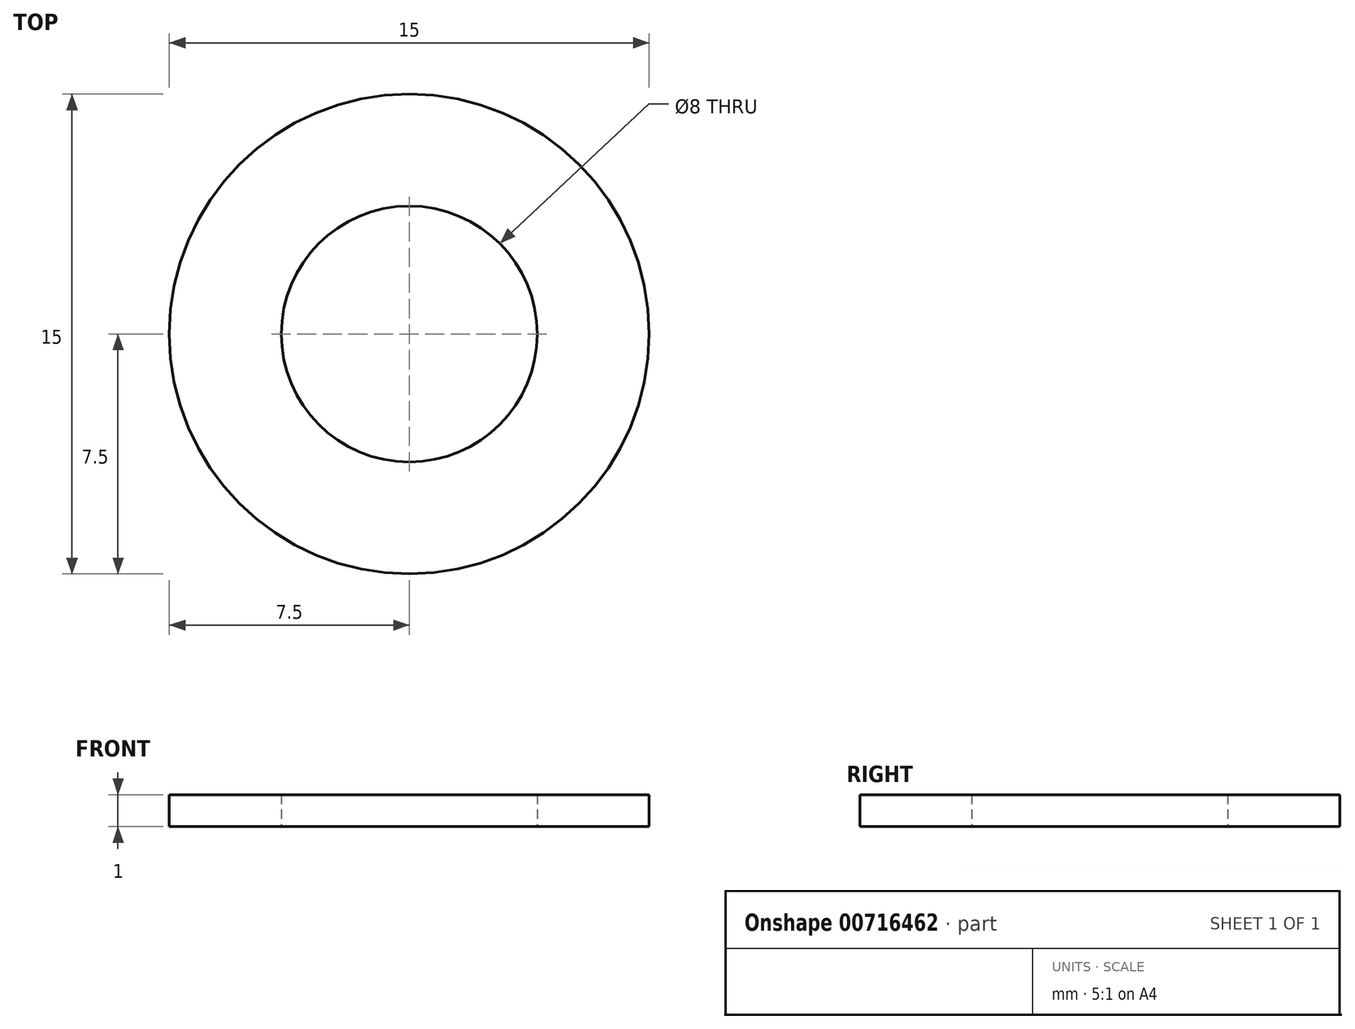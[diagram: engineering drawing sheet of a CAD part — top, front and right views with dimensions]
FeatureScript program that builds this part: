
annotation { "Feature Type Name" : "Feature", "Feature Type Description" : "" }
export const myFeature = defineFeature(function(context is Context, id is Id, definition is map)
    precondition{}
    {
        {
            var Q0;
            Q0=qCreatedBy(makeId("Top.planeOp"),FACE);
            var sketch = newSketch(context, id + "F0", { "sketchPlane" : qUnion([Q0])});
            skCircle(sketch, "E0", {"center": v(0, 0) * mm, "radius": 4 * mm});
            skCircle(sketch, "E1", {"center": v(0, 0) * mm, "radius": 7.5 * mm});
            skSolve(sketch);
        }
        {
            var Q0;
            Q0=makeQuery(id+"F0.imprint","IMPRINT",FACE,{"disambiguationData":[TD([[makeQuery(id+"F0.imprint","IMPRINT",EDGE,{"derivedFrom":sQuery(id+"F0.wireOp",EDGE,"E0")}),-1.0]])]});
            extrude(context, id + "F1", {"entities" : qUnion([Q0]), "depth" : 1 * mm, "offsetDistance" : 25 * mm});
        }
    });
